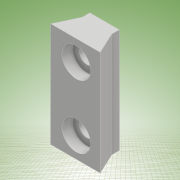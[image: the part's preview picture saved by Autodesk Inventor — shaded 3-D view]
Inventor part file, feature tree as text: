
AUTODESK INVENTOR PART (.ipt)
format: ipt  version: 2017 (Build 210142000, 142)  size: 134,144 bytes
history: native  units: mm
features: hole x2, extrude x1, sketch x1
ambient origin geometry x8: Origin, YZ Plane, XZ Plane, XY Plane, X Axis, Y Axis, Z Axis, Center Point
bodies: Solid1 (feature_tree)
feature tree (4):
  extrude  "Extrusion1"  Depth=2.6mm
  hole  "Hole1"  [1 undecoded]
  hole  "Hole2"  [1 undecoded]
  sketch  "Sketch1"  dims[d4=25.4mm d5=0.0mm d6=5.842mm d30=5.0mm d8=3.6mm d9=6.0mm d10=7.0mm d11=2.6mm d12=90.0deg d13=8.0mm d14=20.594885mm d20=12.7mm d22=5.5mm d23=5.5mm d24=2.0mm d25=2.0mm d28=0.2mm d29=27.052603mm d31=27.052603mm d32=5.842mm d33=5.0mm d34=3.6mm d35=6.0mm d36=7.0mm d37=2.6mm d38=90.0deg d39=8.0mm d40=20.594885mm]
note: 2 required parameter values undecoded (feature->parameter linkage not recoverable at this tier; creation-order binding heuristic only, values carry confidence <= 0.55)
